# Revit family: 1407xxx Micro Recess Unswitched (ETL)
name_source: partatom
category: Lighting Fixtures
revit_build: Autodesk Revit 2018 (Build: 20170223_1515(x64)
units: mm (PartAtom-declared; Revit-internal decimal feet)

## family parameters
Always vertical = Yes
Cut with Voids When Loaded = No
Host = Wall
Light Source = Yes
OmniClass Number = 23.80.70.00
OmniClass Title = Lighting
Part Type = Normal
Room Calculation Point = No
Round Connector Dimension = Use Diameter
Shared = No

## types (2) — shared parameters
Color Filter = 16777215
Dimmable = Yes
Dimming Lamp Color Temperature Shift = <None>
Dimming Method = Control Gear Dependent
Driver Required = Constant Current 700mA
Lamp = LED
Length of Cable Supplied = 1000-1050mm
Light Source Fixed = Yes
Main Finish = Matt White
Main Material = Metal - Aluminium
Manufacturer = Astro Lighting Ltd
Photometric Web File = IES_L17948 Micro Recess Unswitched Luminaire.ies
Product Code = 8629
Product Location = Indoor
Product Name = Micro Recess Unswitched
Product SKU = 1407011
Tilt Angle = 90.00°
URL = www.astrolighting.com

## per-type parameters (varying)
| type | ADA compliant | Apparent Load | Driver Included | Efficacy (lm/w) | Electrical Class | Location rating | Power (Watts) | Wattage Comments |
| CE |  | 6 VA | No | Control Gear Dependent | CE (Class | IP20 | Control Gear Dependent | Measured Wattage. (2W LED Rated) |
| ETL | Yes | 0 VA | Not Applicable | Constant Current 700mA | cETLus (Class 2) | DAMP | 2W | Rated Value |

## geometry (parser evidence)
native form markers: Sweep x1
no freeform markers — native parametric forms only
